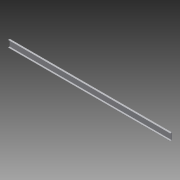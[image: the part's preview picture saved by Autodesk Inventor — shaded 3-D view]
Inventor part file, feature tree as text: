
AUTODESK INVENTOR PART (.ipt)
format: ipt  version: 2013 (Build 170138000, 138)  size: 83,968 bytes
history: native  units: in
note: dims shown in document units (in); Inventor stores cm internally (conversion verified against a paired STEP export)
features: other x2, extrude x1, sketch x1
ambient origin geometry x8: Origin, YZ Plane, XZ Plane, XY Plane, X Axis, Y Axis, Z Axis, Center Point
bodies: Solid1 (feature_tree)
feature tree (4):
  other  "Table"
  other  "Part1-01"
  extrude  "Extrusion1"  Depth=1.0in
  sketch  "Sketch1"  dims[d0=4.0in d1=1.0in d2=0.125in d4=0.0in]
